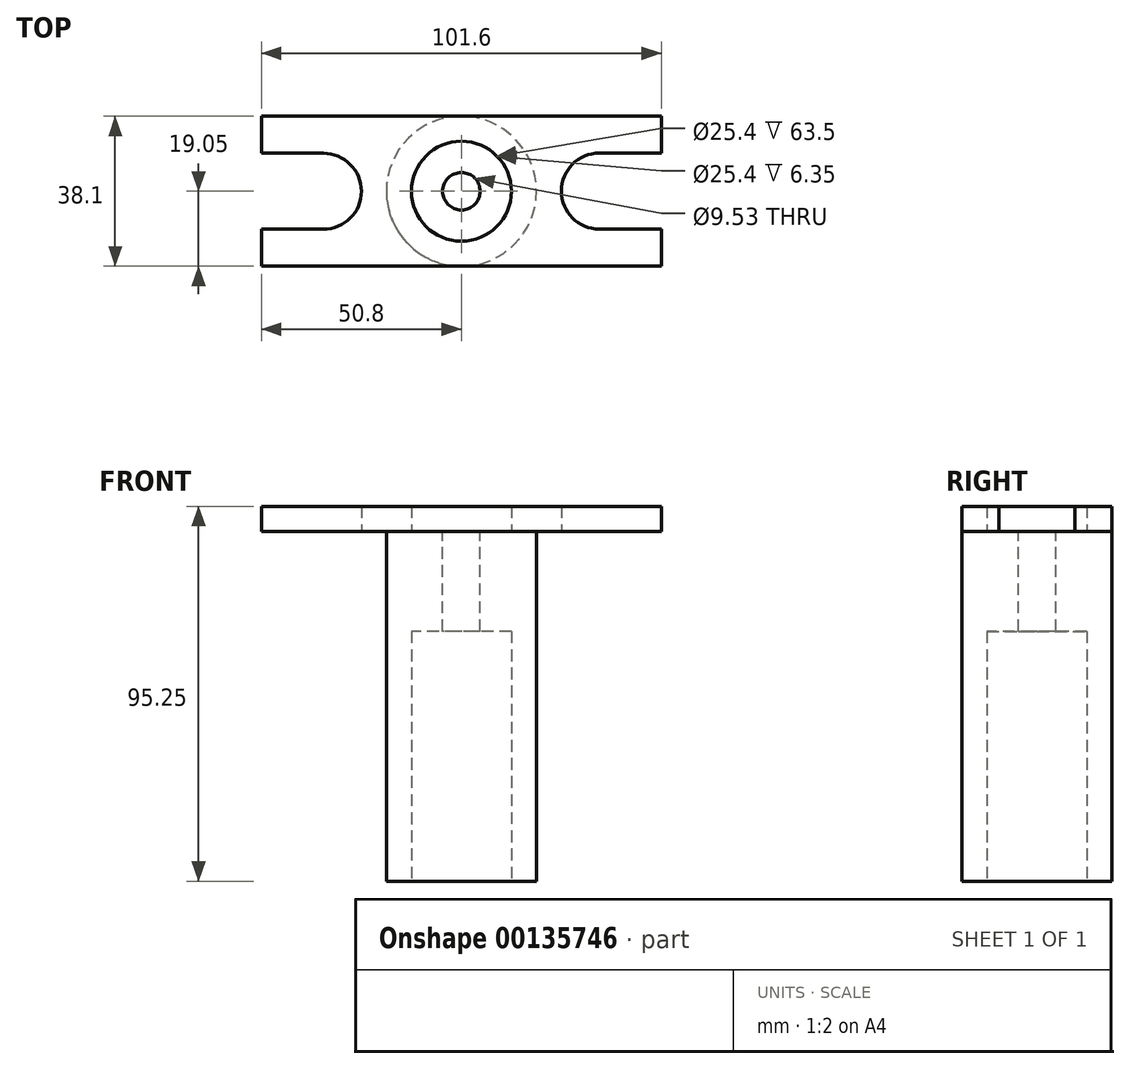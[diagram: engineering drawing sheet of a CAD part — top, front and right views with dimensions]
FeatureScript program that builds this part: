
annotation { "Feature Type Name" : "Feature", "Feature Type Description" : "" }
export const myFeature = defineFeature(function(context is Context, id is Id, definition is map)
    precondition{}
    {
        {
            var Q0;
            Q0=qCreatedBy(makeId("Top.planeOp"),FACE);
            var sketch = newSketch(context, id + "F0", { "sketchPlane" : qUnion([Q0])});
            skLineSegment(sketch, "E0", {"start": v(0, 0) * mm, "end": v(101.6, 0) * mm});
            skLineSegment(sketch, "E1", {"start": v(0, 38.1) * mm, "end": v(101.6, 38.1) * mm});
            skLineSegment(sketch, "E2", {"start": v(101.6, 38.1) * mm, "end": v(101.6, 28.75) * mm});
            skLineSegment(sketch, "E3", {"start": v(0, 38.1) * mm, "end": v(50.8, 38.1) * mm});
            skCircle(sketch, "E4", {"center": v(50.8, 19.05) * mm, "radius": 12.7 * mm});
            skArc(sketch, "E5", {"start": v(15.75, 28.7) * mm, "mid": v(25.4, 19.05) * mm, "end": v(15.75, 9.4) * mm});
            skArc(sketch, "E6", {"start": v(85.85, 28.75) * mm, "mid": v(76.2, 19.1) * mm, "end": v(85.85, 9.44) * mm});
            skLineSegment(sketch, "E7", {"start": v(85.85, 9.44) * mm, "end": v(101.6, 9.44) * mm});
            skLineSegment(sketch, "E8", {"start": v(85.85, 28.75) * mm, "end": v(101.6, 28.75) * mm});
            skLineSegment(sketch, "E9", {"start": v(15.75, 28.7) * mm, "end": v(0, 28.7) * mm});
            skLineSegment(sketch, "E10", {"start": v(15.75, 9.4) * mm, "end": v(0, 9.4) * mm});
            skLineSegment(sketch, "E11.trimOffspring", {"start": v(0, 28.7) * mm, "end": v(0, 38.1) * mm});
            skLineSegment(sketch, "E12.trimOffspring", {"start": v(101.6, 9.44) * mm, "end": v(101.6, 0) * mm});
            skLineSegment(sketch, "E13", {"start": v(0, 0) * mm, "end": v(0, 9.4) * mm});
            skSolve(sketch);
        }
        {
            var Q0;
            Q0 = qSketchRegion(id + "F0", true);
            extrude(context, id + "F1", {"entities" : qUnion([Q0]), "depth" : 6.35 * mm});
        }
        {
            var Q0;
            Q0=makeQuery(id+"F1.opExtrude","CAP_FACE",FACE,{"disambiguationData":[OSD([sQuery(id+"F0.wireOp",EDGE,"E0"),sQuery(id+"F0.wireOp",EDGE,"E1"),sQuery(id+"F0.wireOp",EDGE,"E3"),sQuery(id+"F0.wireOp",EDGE,"E2"),sQuery(id+"F0.wireOp",EDGE,"E4"),sQuery(id+"F0.wireOp",EDGE,"E5"),sQuery(id+"F0.wireOp",EDGE,"E6"),sQuery(id+"F0.wireOp",EDGE,"E7"),sQuery(id+"F0.wireOp",EDGE,"E8"),sQuery(id+"F0.wireOp",EDGE,"E9"),sQuery(id+"F0.wireOp",EDGE,"E10"),sQuery(id+"F0.wireOp",EDGE,"E11.trimOffspring"),sQuery(id+"F0.wireOp",EDGE,"E12.trimOffspring"),sQuery(id+"F0.wireOp",EDGE,"E13")])],"isStart":true});
            var sketch = newSketch(context, id + "F2", { "sketchPlane" : qUnion([Q0])});
            skCircle(sketch, "E14", {"center": v(50.8, -19.05) * mm, "radius": 19.05 * mm});
            skCircle(sketch, "E15", {"center": v(50.8, -19.05) * mm, "radius": 4.76 * mm});
            skSolve(sketch);
        }
        {
            var Q0;
            Q0=makeQuery(id+"F2.imprint","IMPRINT",FACE,{"disambiguationData":[TD([[makeQuery(id+"F2.imprint","IMPRINT",EDGE,{"derivedFrom":makeQuery(id+"F1.opExtrude","CAP_EDGE",EDGE,{"disambiguationData":[OSD([sQuery(id+"F0.wireOp",EDGE,"E4")])],"isStart":true})}),1.0]])]});
            extrude(context, id + "F3", {"entities" : qUnion([Q0]), "operationType" : NewBodyOperationType.ADD, "depth" : 63.5 * mm});
        }
        {
            var Q0;
            Q0=qCreatedBy(makeId("Top.planeOp"),FACE);
            var sketch = newSketch(context, id + "F4", { "sketchPlane" : qUnion([Q0])});
            skCircle(sketch, "E16.0.0", {"center": v(50.8, 19.05) * mm, "radius": 19.05 * mm});
            skCircle(sketch, "E17", {"center": v(50.8, 19.05) * mm, "radius": 4.76 * mm});
            skSolve(sketch);
        }
        {
            var Q0;
            Q0=makeQuery(id+"F3.opExtrude","CAP_FACE",FACE,{"disambiguationData":[OSD([sQuery(id+"F0.wireOp",EDGE,"E4"),sQuery(id+"F2.wireOp",EDGE,"E14")])],"isStart":false});
            var Q1;
            Q1=makeQuery(id+"F4.imprint","IMPRINT",FACE,{"disambiguationData":[TD([[makeQuery(id+"F4.imprint","IMPRINT",EDGE,{"derivedFrom":sQuery(id+"F4.wireOp",EDGE,"E16.0.0")}),1.0]])]});
            extrude(context, id + "F5", {"entities" : qUnion([Q0, Q1]), "operationType" : NewBodyOperationType.ADD, "depth" : 25.4 * mm});
        }
    });
